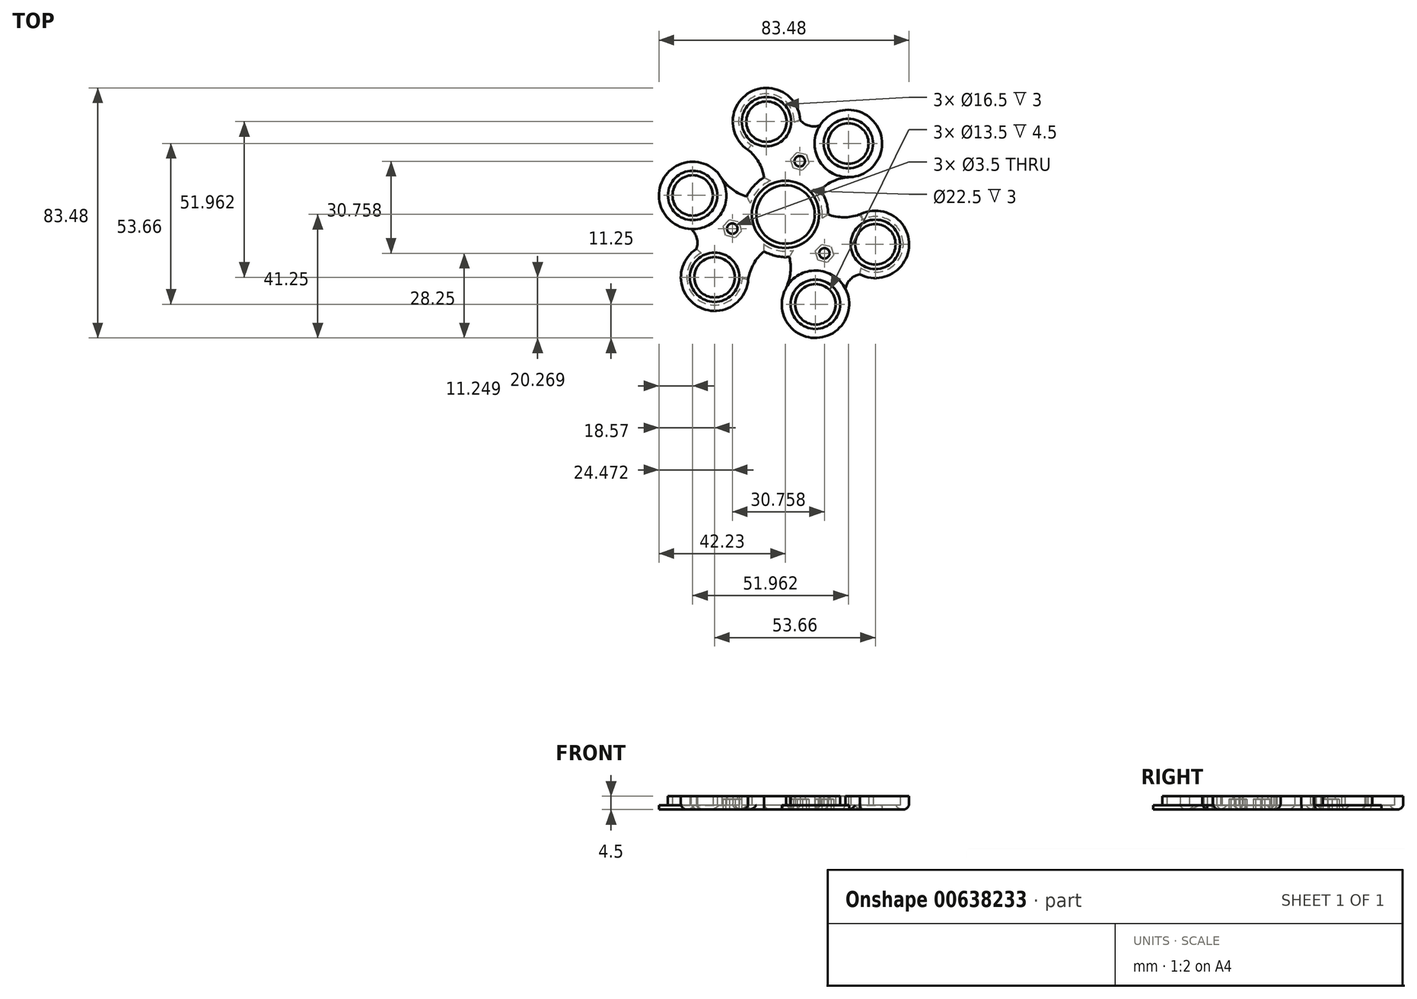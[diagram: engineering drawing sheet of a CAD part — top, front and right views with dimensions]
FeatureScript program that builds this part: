
annotation { "Feature Type Name" : "Feature", "Feature Type Description" : "" }
export const myFeature = defineFeature(function(context is Context, id is Id, definition is map)
    precondition{}
    {
        {
            assignVariable(context, id + "F0", {"name" : "OuterBearingHeight", "anyValue" : 5});
        }
        {
            assignVariable(context, id + "F1", {"name" : "CenterBearingHeight", "anyValue" : 7});
        }
        {
            var Q0;
            Q0=qCreatedBy(makeId("Top.planeOp"),FACE);
            var sketch = newSketch(context, id + "F2", { "sketchPlane" : qUnion([Q0])});
            skCircle(sketch, "E0", {"center": v(0, 0) * mm, "radius": 11.25 * mm});
            skCircle(sketch, "E1", {"center": v(0, 0) * mm, "radius": 9.75 * mm});
            skCircle(sketch, "E2", {"center": v(30, -10) * mm, "radius": 8.25 * mm});
            skCircle(sketch, "E3", {"center": v(30, -10) * mm, "radius": 6.75 * mm});
            skCircle(sketch, "E4", {"center": v(0, 0) * mm, "radius": 14.25 * mm});
            skCircle(sketch, "E5", {"center": v(30, -10) * mm, "radius": 11.25 * mm});
            skArc(sketch, "E6", {"start": v(14.25, 0) * mm, "mid": v(19.63, -0.96) * mm, "end": v(25, 0.08) * mm});
            skCircle(sketch, "E7.MirrorC", {"center": v(10, -30) * mm, "radius": 11.25 * mm});
            skCircle(sketch, "E8.MirrorC", {"center": v(10, -30) * mm, "radius": 8.25 * mm});
            skCircle(sketch, "E9.MirrorC", {"center": v(10, -30) * mm, "radius": 6.75 * mm});
            skArc(sketch, "E10.MirrorCS", {"start": v(1.27, -14.2) * mm, "mid": v(1.6, -19.87) * mm, "end": v(-0.2, -25.25) * mm});
            skArc(sketch, "E11", {"start": v(24.85, -20) * mm, "mid": v(21.66, -21.66) * mm, "end": v(20, -24.85) * mm});
            skCircle(sketch, "E12", {"center": v(13, -13) * mm, "radius": 1.75 * mm});
            skCircle(sketch, "E13.cCircle", {"center": v(13, -13) * mm, "radius": 2.75 * mm, "construction": true});
            skLineSegment(sketch, "E13.0", {"start": v(13.92, -16.04) * mm, "end": v(10.83, -15.31) * mm});
            skLineSegment(sketch, "E13.1", {"start": v(10.83, -15.31) * mm, "end": v(9.9, -12.27) * mm});
            skLineSegment(sketch, "E13.2", {"start": v(9.9, -12.27) * mm, "end": v(12.08, -9.96) * mm});
            skLineSegment(sketch, "E13.3", {"start": v(12.08, -9.96) * mm, "end": v(15.17, -10.69) * mm});
            skLineSegment(sketch, "E13.4", {"start": v(15.17, -10.69) * mm, "end": v(16.1, -13.73) * mm});
            skLineSegment(sketch, "E13.5", {"start": v(16.1, -13.73) * mm, "end": v(13.92, -16.04) * mm});
            skLineSegment(sketch, "E14.1.0", {"start": v(6.93, 20.07) * mm, "end": v(7.85, 17.03) * mm});
            skCircle(sketch, "E14.1.1", {"center": v(4.76, 17.76) * mm, "radius": 2.75 * mm, "construction": true});
            skLineSegment(sketch, "E14.1.2", {"start": v(7.85, 17.03) * mm, "end": v(5.67, 14.72) * mm});
            skLineSegment(sketch, "E14.1.3", {"start": v(5.67, 14.72) * mm, "end": v(2.58, 15.44) * mm});
            skLineSegment(sketch, "E14.1.4", {"start": v(2.58, 15.44) * mm, "end": v(1.67, 18.48) * mm});
            skLineSegment(sketch, "E14.1.5", {"start": v(1.67, 18.48) * mm, "end": v(3.84, 20.8) * mm});
            skLineSegment(sketch, "E14.1.6", {"start": v(3.84, 20.8) * mm, "end": v(6.93, 20.07) * mm});
            skCircle(sketch, "E14.1.7", {"center": v(-6.34, 30.98) * mm, "radius": 6.75 * mm});
            skCircle(sketch, "E14.1.8", {"center": v(-6.34, 30.98) * mm, "radius": 8.25 * mm});
            skCircle(sketch, "E14.1.9", {"center": v(-6.34, 30.98) * mm, "radius": 11.25 * mm});
            skArc(sketch, "E14.1.10", {"start": v(4.9, 31.52) * mm, "mid": v(7.93, 29.6) * mm, "end": v(11.52, 29.74) * mm});
            skArc(sketch, "E14.1.11", {"start": v(-7.12, 12.34) * mm, "mid": v(-8.99, 17.48) * mm, "end": v(-12.57, 21.61) * mm});
            skArc(sketch, "E14.1.12", {"start": v(11.66, 8.2) * mm, "mid": v(16.4, 11.32) * mm, "end": v(21.97, 12.45) * mm});
            skCircle(sketch, "E14.1.13", {"center": v(20.98, 23.66) * mm, "radius": 11.25 * mm});
            skCircle(sketch, "E14.1.14", {"center": v(20.98, 23.66) * mm, "radius": 8.25 * mm});
            skCircle(sketch, "E14.1.15", {"center": v(20.98, 23.66) * mm, "radius": 6.75 * mm});
            skLineSegment(sketch, "E14.2.0", {"start": v(-20.85, -4.03) * mm, "end": v(-18.67, -1.72) * mm});
            skCircle(sketch, "E14.2.1", {"center": v(-17.76, -4.76) * mm, "radius": 2.75 * mm, "construction": true});
            skLineSegment(sketch, "E14.2.2", {"start": v(-18.67, -1.72) * mm, "end": v(-15.58, -2.44) * mm});
            skLineSegment(sketch, "E14.2.3", {"start": v(-15.58, -2.44) * mm, "end": v(-14.67, -5.48) * mm});
            skLineSegment(sketch, "E14.2.4", {"start": v(-14.67, -5.48) * mm, "end": v(-16.84, -7.8) * mm});
            skLineSegment(sketch, "E14.2.5", {"start": v(-16.84, -7.8) * mm, "end": v(-19.93, -7.07) * mm});
            skLineSegment(sketch, "E14.2.6", {"start": v(-19.93, -7.07) * mm, "end": v(-20.85, -4.03) * mm});
            skCircle(sketch, "E14.2.7", {"center": v(-23.66, -20.98) * mm, "radius": 6.75 * mm});
            skCircle(sketch, "E14.2.8", {"center": v(-23.66, -20.98) * mm, "radius": 8.25 * mm});
            skCircle(sketch, "E14.2.9", {"center": v(-23.66, -20.98) * mm, "radius": 11.25 * mm});
            skArc(sketch, "E14.2.10", {"start": v(-29.74, -11.52) * mm, "mid": v(-29.6, -7.93) * mm, "end": v(-31.52, -4.9) * mm});
            skArc(sketch, "E14.2.11", {"start": v(-7.13, -12.34) * mm, "mid": v(-10.65, -16.52) * mm, "end": v(-12.43, -21.69) * mm});
            skArc(sketch, "E14.2.12", {"start": v(-12.93, 6) * mm, "mid": v(-18, 8.55) * mm, "end": v(-21.77, 12.8) * mm});
            skCircle(sketch, "E14.2.13", {"center": v(-30.98, 6.34) * mm, "radius": 11.25 * mm});
            skCircle(sketch, "E14.2.14", {"center": v(-30.98, 6.34) * mm, "radius": 8.25 * mm});
            skCircle(sketch, "E14.2.15", {"center": v(-30.98, 6.34) * mm, "radius": 6.75 * mm});
            skCircle(sketch, "E15", {"center": v(-17.76, -4.76) * mm, "radius": 1.75 * mm});
            skCircle(sketch, "E16", {"center": v(4.76, 17.76) * mm, "radius": 1.75 * mm});
            skSolve(sketch);
        }
        {
            var Q0;
            Q0=makeQuery(id+"F2.imprint","IMPRINT",FACE,{"disambiguationData":[TD([[makeQuery(id+"F2.imprint","IMPRINT",EDGE,{"derivedFrom":sQuery(id+"F2.wireOp",EDGE,"E0")}),-1.0]])]});
            var Q1;
            Q1=makeQuery(id+"F2.imprint","IMPRINT",FACE,{"disambiguationData":[TD([[makeQuery(id+"F2.imprint","IMPRINT",EDGE,{"derivedFrom":sQuery(id+"F2.wireOp",EDGE,"8bcb8120-0ba0-4aea-ab6e-afe790873060.2.4")}),1.0]])]});
            var Q2;
            Q2=makeQuery(id+"F2.imprint","IMPRINT",FACE,{"disambiguationData":[TD([[makeQuery(id+"F2.imprint","IMPRINT",EDGE,{"derivedFrom":sQuery(id+"F2.wireOp",EDGE,"77096406-894a-42e3-b711-8bd3589b9249.0")}),1.0]])]});
            var Q3;
            Q3=makeQuery(id+"F2.imprint","IMPRINT",FACE,{"disambiguationData":[TD([[makeQuery(id+"F2.imprint","IMPRINT",EDGE,{"derivedFrom":sQuery(id+"F2.wireOp",EDGE,"8bcb8120-0ba0-4aea-ab6e-afe790873060.2.11")}),-1.0]])]});
            var Q4;
            Q4=makeQuery(id+"F2.imprint","IMPRINT",FACE,{"disambiguationData":[TD([[makeQuery(id+"F2.imprint","IMPRINT",EDGE,{"derivedFrom":sQuery(id+"F2.wireOp",EDGE,"8bcb8120-0ba0-4aea-ab6e-afe790873060.1.4")}),1.0]])]});
            var Q5;
            Q5=makeQuery(id+"F2.imprint","IMPRINT",FACE,{"disambiguationData":[TD([[makeQuery(id+"F2.imprint","IMPRINT",EDGE,{"derivedFrom":sQuery(id+"F2.wireOp",EDGE,"8bcb8120-0ba0-4aea-ab6e-afe790873060.1.11")}),-1.0]])]});
            var Q6;
            Q6=makeQuery(id+"F2.imprint","IMPRINT",FACE,{"disambiguationData":[TD([[makeQuery(id+"F2.imprint","IMPRINT",EDGE,{"derivedFrom":sQuery(id+"F2.wireOp",EDGE,"E2")}),-1.0]])]});
            var Q7;
            {var subQ0=sQuery(id+"F2.wireOp",EDGE,"aIkXae3d-mRoF-3wDr-qNRh-ahO2MIR5sPZY");var subQ1=sQuery(id+"F2.wireOp",EDGE,"E5");var subQ2=makeQuery(id+"F2.imprint","INTERSECT",VERTEX,{"disambiguationData":[OD(0.0)],"derivedFrom":[subQ1,subQ0]});Q7=makeQuery(id+"F2.imprint","IMPRINT",FACE,{"disambiguationData":[TD([[makeQuery(id+"F2.imprint","IMPRINT",EDGE,{"disambiguationData":[TD([[subQ2,1.0]])],"derivedFrom":subQ1}),1.0]])]});}
            var Q8;
            {var subQ0=sQuery(id+"F2.wireOp",EDGE,"8bcb8120-0ba0-4aea-ab6e-afe790873060.2.2");var subQ1=sQuery(id+"F2.wireOp",EDGE,"8bcb8120-0ba0-4aea-ab6e-afe790873060.2.1");var subQ2=makeQuery(id+"F2.imprint","INTERSECT",VERTEX,{"disambiguationData":[OD(0.0)],"derivedFrom":[subQ1,subQ0]});Q8=makeQuery(id+"F2.imprint","IMPRINT",FACE,{"disambiguationData":[TD([[makeQuery(id+"F2.imprint","IMPRINT",EDGE,{"disambiguationData":[TD([[subQ2,1.0]])],"derivedFrom":subQ1}),-1.0]])]});}
            var Q9;
            {var subQ0=sQuery(id+"F2.wireOp",EDGE,"8bcb8120-0ba0-4aea-ab6e-afe790873060.1.2");var subQ1=sQuery(id+"F2.wireOp",EDGE,"8bcb8120-0ba0-4aea-ab6e-afe790873060.1.1");var subQ2=makeQuery(id+"F2.imprint","INTERSECT",VERTEX,{"disambiguationData":[OD(0.0)],"derivedFrom":[subQ1,subQ0]});Q9=makeQuery(id+"F2.imprint","IMPRINT",FACE,{"disambiguationData":[TD([[makeQuery(id+"F2.imprint","IMPRINT",EDGE,{"disambiguationData":[TD([[subQ2,1.0]])],"derivedFrom":subQ1}),-1.0]])]});}
            var Q10;
            Q10=makeQuery(id+"F2.imprint","IMPRINT",FACE,{"disambiguationData":[TD([[makeQuery(id+"F2.imprint","IMPRINT",EDGE,{"derivedFrom":sQuery(id+"F2.wireOp",EDGE,"E8.MirrorC")}),1.0]])]});
            var Q11;
            {var subQ5=sQuery(id+"F2.wireOp",EDGE,"E11");Q11=makeQuery(id+"F2.imprint","IMPRINT",FACE,{"disambiguationData":[TD([[makeQuery(id+"F2.imprint","IMPRINT",EDGE,{"derivedFrom":subQ5}),-1.0]])]});}
            var Q12;
            Q12=makeQuery(id+"F2.imprint","IMPRINT",FACE,{"disambiguationData":[TD([[makeQuery(id+"F2.imprint","IMPRINT",EDGE,{"derivedFrom":sQuery(id+"F2.wireOp",EDGE,"E14.2.0")}),1.0]])]});
            var Q13;
            Q13=makeQuery(id+"F2.imprint","IMPRINT",FACE,{"disambiguationData":[TD([[makeQuery(id+"F2.imprint","IMPRINT",EDGE,{"derivedFrom":sQuery(id+"F2.wireOp",EDGE,"E14.1.0")}),1.0]])]});
            var Q14;
            Q14=makeQuery(id+"F2.imprint","IMPRINT",FACE,{"disambiguationData":[TD([[makeQuery(id+"F2.imprint","IMPRINT",EDGE,{"derivedFrom":sQuery(id+"F2.wireOp",EDGE,"E14.1.8")}),-1.0]])]});
            var Q15;
            Q15=makeQuery(id+"F2.imprint","IMPRINT",FACE,{"disambiguationData":[TD([[makeQuery(id+"F2.imprint","IMPRINT",EDGE,{"derivedFrom":sQuery(id+"F2.wireOp",EDGE,"E14.2.14")}),1.0]])]});
            var Q16;
            Q16=makeQuery(id+"F2.imprint","IMPRINT",FACE,{"disambiguationData":[TD([[makeQuery(id+"F2.imprint","IMPRINT",EDGE,{"derivedFrom":sQuery(id+"F2.wireOp",EDGE,"E14.2.8")}),-1.0]])]});
            var Q17;
            Q17=makeQuery(id+"F2.imprint","IMPRINT",FACE,{"disambiguationData":[TD([[makeQuery(id+"F2.imprint","IMPRINT",EDGE,{"derivedFrom":sQuery(id+"F2.wireOp",EDGE,"E14.1.14")}),1.0]])]});
            var Q18;
            {var subQ0=sQuery(id+"F2.wireOp",EDGE,"E10.MirrorCS");var subQ1=sQuery(id+"F2.wireOp",EDGE,"E7.MirrorC");var subQ2=makeQuery(id+"F2.imprint","INTERSECT",VERTEX,{"disambiguationData":[OD(0.0)],"derivedFrom":[subQ1,subQ0]});Q18=makeQuery(id+"F2.imprint","IMPRINT",FACE,{"disambiguationData":[TD([[makeQuery(id+"F2.imprint","IMPRINT",EDGE,{"disambiguationData":[TD([[subQ2,-1.0]])],"derivedFrom":subQ1}),-1.0]])]});}
            var Q19;
            {var subQ0=sQuery(id+"F2.wireOp",EDGE,"E14.2.13");var subQ1=sQuery(id+"F2.wireOp",EDGE,"E14.2.12");var subQ2=makeQuery(id+"F2.imprint","INTERSECT",VERTEX,{"disambiguationData":[OD(0.0)],"derivedFrom":[subQ1,subQ0]});Q19=makeQuery(id+"F2.imprint","IMPRINT",FACE,{"disambiguationData":[TD([[makeQuery(id+"F2.imprint","IMPRINT",EDGE,{"disambiguationData":[TD([[subQ2,1.0]])],"derivedFrom":subQ1}),-1.0]])]});}
            var Q20;
            {var subQ0=sQuery(id+"F2.wireOp",EDGE,"E14.1.13");var subQ1=sQuery(id+"F2.wireOp",EDGE,"E14.1.12");var subQ2=makeQuery(id+"F2.imprint","INTERSECT",VERTEX,{"disambiguationData":[OD(0.0)],"derivedFrom":[subQ1,subQ0]});Q20=makeQuery(id+"F2.imprint","IMPRINT",FACE,{"disambiguationData":[TD([[makeQuery(id+"F2.imprint","IMPRINT",EDGE,{"disambiguationData":[TD([[subQ2,1.0]])],"derivedFrom":subQ1}),-1.0]])]});}
            var Q21;
            {var subQ3=sQuery(id+"F2.wireOp",EDGE,"E4");var subQ5=sQuery(id+"F2.wireOp",EDGE,"E10.MirrorCS");var subQ9=makeQuery(id+"F2.imprint","INTERSECT",VERTEX,{"derivedFrom":[subQ3,subQ5]});Q21=makeQuery(id+"F2.imprint","IMPRINT",FACE,{"disambiguationData":[TD([[makeQuery(id+"F2.imprint","IMPRINT",EDGE,{"disambiguationData":[TD([[subQ9,-1.0]])],"derivedFrom":subQ3}),-1.0]])]});}
            var Q22;
            {var subQ6=sQuery(id+"F2.wireOp",EDGE,"E14.2.3");Q22=makeQuery(id+"F2.imprint","IMPRINT",FACE,{"disambiguationData":[TD([[makeQuery(id+"F2.imprint","IMPRINT",EDGE,{"derivedFrom":subQ6}),1.0]])]});}
            var Q23;
            {var subQ0=sQuery(id+"F2.wireOp",EDGE,"E14.1.3");Q23=makeQuery(id+"F2.imprint","IMPRINT",FACE,{"disambiguationData":[TD([[makeQuery(id+"F2.imprint","IMPRINT",EDGE,{"derivedFrom":subQ0}),1.0]])]});}
            extrude(context, id + "F3", {"entities" : qUnion([Q0, Q1, Q2, Q3, Q4, Q5, Q6, Q7, Q8, Q9, Q10, Q11, Q12, Q13, Q14, Q15, Q16, Q17, Q18, Q19, Q20, Q21, Q22, Q23]), "depth" : ((getVariable(context, 'CenterBearingHeight') / 2) + 1) * mm, "offsetDistance" : 25 * mm});
        }
        {
            var Q0;
            Q0=makeQuery(id+"F2.imprint","IMPRINT",FACE,{"disambiguationData":[TD([[makeQuery(id+"F2.imprint","IMPRINT",EDGE,{"derivedFrom":sQuery(id+"F2.wireOp",EDGE,"E2")}),1.0]])]});
            var Q1;
            Q1=makeQuery(id+"F2.imprint","IMPRINT",FACE,{"disambiguationData":[TD([[makeQuery(id+"F2.imprint","IMPRINT",EDGE,{"derivedFrom":sQuery(id+"F2.wireOp",EDGE,"8bcb8120-0ba0-4aea-ab6e-afe790873060.2.11")}),1.0]])]});
            var Q2;
            Q2=makeQuery(id+"F2.imprint","IMPRINT",FACE,{"disambiguationData":[TD([[makeQuery(id+"F2.imprint","IMPRINT",EDGE,{"derivedFrom":sQuery(id+"F2.wireOp",EDGE,"8bcb8120-0ba0-4aea-ab6e-afe790873060.1.11")}),1.0]])]});
            var Q3;
            Q3=makeQuery(id+"F2.imprint","IMPRINT",FACE,{"disambiguationData":[TD([[makeQuery(id+"F2.imprint","IMPRINT",EDGE,{"derivedFrom":sQuery(id+"F2.wireOp",EDGE,"E14.1.7")}),-1.0]])]});
            var Q4;
            Q4=makeQuery(id+"F2.imprint","IMPRINT",FACE,{"disambiguationData":[TD([[makeQuery(id+"F2.imprint","IMPRINT",EDGE,{"derivedFrom":sQuery(id+"F2.wireOp",EDGE,"E14.1.14")}),-1.0]])]});
            var Q5;
            Q5=makeQuery(id+"F2.imprint","IMPRINT",FACE,{"disambiguationData":[TD([[makeQuery(id+"F2.imprint","IMPRINT",EDGE,{"derivedFrom":sQuery(id+"F2.wireOp",EDGE,"E8.MirrorC")}),-1.0]])]});
            var Q6;
            Q6=makeQuery(id+"F2.imprint","IMPRINT",FACE,{"disambiguationData":[TD([[makeQuery(id+"F2.imprint","IMPRINT",EDGE,{"derivedFrom":sQuery(id+"F2.wireOp",EDGE,"E14.2.7")}),-1.0]])]});
            var Q7;
            Q7=makeQuery(id+"F2.imprint","IMPRINT",FACE,{"disambiguationData":[TD([[makeQuery(id+"F2.imprint","IMPRINT",EDGE,{"derivedFrom":sQuery(id+"F2.wireOp",EDGE,"E0")}),1.0]])]});
            var Q8;
            Q8=makeQuery(id+"F2.imprint","IMPRINT",FACE,{"disambiguationData":[TD([[makeQuery(id+"F2.imprint","IMPRINT",EDGE,{"derivedFrom":sQuery(id+"F2.wireOp",EDGE,"E14.2.14")}),-1.0]])]});
            extrude(context, id + "F4", {"entities" : qUnion([Q0, Q1, Q2, Q3, Q4, Q5, Q6, Q7, Q8]), "operationType" : NewBodyOperationType.ADD, "depth" : (((getVariable(context, 'CenterBearingHeight') / 2) + .5) - getVariable(context, 'OuterBearingHeight') / 2) * mm, "offsetDistance" : 25 * mm});
        }
        {
            var Q0;
            Q0=makeQuery(id+"F2.imprint","IMPRINT",FACE,{"disambiguationData":[TD([[makeQuery(id+"F2.imprint","IMPRINT",EDGE,{"derivedFrom":sQuery(id+"F2.wireOp",EDGE,"8bcb8120-0ba0-4aea-ab6e-afe790873060.2.4")}),-1.0]])]});
            var Q1;
            Q1=makeQuery(id+"F2.imprint","IMPRINT",FACE,{"disambiguationData":[TD([[makeQuery(id+"F2.imprint","IMPRINT",EDGE,{"derivedFrom":sQuery(id+"F2.wireOp",EDGE,"mnrSd04r-Lz4n-X5wf-1ZHD-ls6KPZvvDbA1")}),-1.0]])]});
            var Q2;
            Q2=makeQuery(id+"F2.imprint","IMPRINT",FACE,{"disambiguationData":[TD([[makeQuery(id+"F2.imprint","IMPRINT",EDGE,{"derivedFrom":sQuery(id+"F2.wireOp",EDGE,"8bcb8120-0ba0-4aea-ab6e-afe790873060.1.4")}),-1.0]])]});
            var Q3;
            {var subQ0=sQuery(id+"F2.wireOp",EDGE,"E14.2.6");var subQ1=sQuery(id+"F2.wireOp",EDGE,"E14.2.5");var subQ2=makeQuery(id+"F2.imprint","INTERSECT",VERTEX,{"derivedFrom":[subQ1,subQ0]});Q3=makeQuery(id+"F2.imprint","IMPRINT",FACE,{"disambiguationData":[TD([[makeQuery(id+"F2.imprint","IMPRINT",EDGE,{"disambiguationData":[TD([[subQ2,1.0]])],"derivedFrom":subQ1}),-1.0]])]});}
            var Q4;
            {var subQ0=sQuery(id+"F2.wireOp",EDGE,"E14.2.3");Q4=makeQuery(id+"F2.imprint","IMPRINT",FACE,{"disambiguationData":[TD([[makeQuery(id+"F2.imprint","IMPRINT",EDGE,{"derivedFrom":subQ0}),-1.0]])]});}
            var Q5;
            {var subQ0=sQuery(id+"F2.wireOp",EDGE,"E14.2.0");var subQ1=sQuery(id+"F2.wireOp",EDGE,"E4");var subQ2=makeQuery(id+"F2.imprint","INTERSECT",VERTEX,{"derivedFrom":[subQ1,subQ0]});Q5=makeQuery(id+"F2.imprint","IMPRINT",FACE,{"disambiguationData":[TD([[makeQuery(id+"F2.imprint","IMPRINT",EDGE,{"disambiguationData":[TD([[subQ2,-1.0]])],"derivedFrom":subQ1}),1.0]])]});}
            var Q6;
            Q6=makeQuery(id+"F2.imprint","IMPRINT",FACE,{"disambiguationData":[TD([[makeQuery(id+"F2.imprint","IMPRINT",EDGE,{"derivedFrom":sQuery(id+"F2.wireOp",EDGE,"E12")}),-1.0]])]});
            var Q7;
            {var subQ0=sQuery(id+"F2.wireOp",EDGE,"E13.5");var subQ1=sQuery(id+"F2.wireOp",EDGE,"E7.MirrorC");var subQ2=makeQuery(id+"F2.imprint","INTERSECT",VERTEX,{"derivedFrom":[subQ1,subQ0]});Q7=makeQuery(id+"F2.imprint","IMPRINT",FACE,{"disambiguationData":[TD([[makeQuery(id+"F2.imprint","IMPRINT",EDGE,{"disambiguationData":[TD([[subQ2,-1.0]])],"derivedFrom":subQ1}),-1.0]])]});}
            var Q8;
            {var subQ0=sQuery(id+"F2.wireOp",EDGE,"E13.0");var subQ1=sQuery(id+"F2.wireOp",EDGE,"E4");var subQ2=makeQuery(id+"F2.imprint","INTERSECT",VERTEX,{"derivedFrom":[subQ1,subQ0]});Q8=makeQuery(id+"F2.imprint","IMPRINT",FACE,{"disambiguationData":[TD([[makeQuery(id+"F2.imprint","IMPRINT",EDGE,{"disambiguationData":[TD([[subQ2,-1.0]])],"derivedFrom":subQ1}),1.0]])]});}
            var Q9;
            {var subQ0=sQuery(id+"F2.wireOp",EDGE,"E14.1.6");var subQ1=sQuery(id+"F2.wireOp",EDGE,"E14.1.5");var subQ2=makeQuery(id+"F2.imprint","INTERSECT",VERTEX,{"derivedFrom":[subQ1,subQ0]});Q9=makeQuery(id+"F2.imprint","IMPRINT",FACE,{"disambiguationData":[TD([[makeQuery(id+"F2.imprint","IMPRINT",EDGE,{"disambiguationData":[TD([[subQ2,1.0]])],"derivedFrom":subQ1}),-1.0]])]});}
            var Q10;
            {var subQ0=sQuery(id+"F2.wireOp",EDGE,"E14.1.3");Q10=makeQuery(id+"F2.imprint","IMPRINT",FACE,{"disambiguationData":[TD([[makeQuery(id+"F2.imprint","IMPRINT",EDGE,{"derivedFrom":subQ0}),-1.0]])]});}
            var Q11;
            {var subQ0=sQuery(id+"F2.wireOp",EDGE,"E14.1.0");var subQ1=sQuery(id+"F2.wireOp",EDGE,"E4");var subQ2=makeQuery(id+"F2.imprint","INTERSECT",VERTEX,{"derivedFrom":[subQ1,subQ0]});Q11=makeQuery(id+"F2.imprint","IMPRINT",FACE,{"disambiguationData":[TD([[makeQuery(id+"F2.imprint","IMPRINT",EDGE,{"disambiguationData":[TD([[subQ2,-1.0]])],"derivedFrom":subQ1}),1.0]])]});}
            extrude(context, id + "F5", {"entities" : qUnion([Q0, Q1, Q2, Q3, Q4, Q5, Q6, Q7, Q8, Q9, Q10, Q11]), "operationType" : NewBodyOperationType.ADD, "depth" : ((getVariable(context, 'CenterBearingHeight') / 2) + 1) * mm, "offsetDistance" : 25 * mm, "hasSecondDirection" : true, "secondDirectionOppositeDirection" : false, "secondDirectionDepth" : 3.5 * mm});
        }
        {
            var Q0;
            Q0=makeQuery(id+"F2.imprint","IMPRINT",FACE,{"disambiguationData":[TD([[makeQuery(id+"F2.imprint","IMPRINT",EDGE,{"derivedFrom":sQuery(id+"F2.wireOp",EDGE,"E0")}),1.0]])]});
            extrude(context, id + "F6", {"entities" : qUnion([Q0]), "operationType" : NewBodyOperationType.ADD, "depth" : 1 * mm, "offsetDistance" : 25 * mm});
        }
        {
            var Q0;
            Q0=makeQuery(id+"F3.opExtrude","CAP_EDGE",EDGE,{"disambiguationData":[OSD([sQuery(id+"F2.wireOp",EDGE,"E14.2.13")])],"isStart":true});
            var Q1;
            Q1=makeQuery(id+"F3.opExtrude","CAP_EDGE",EDGE,{"disambiguationData":[OSD([sQuery(id+"F2.wireOp",EDGE,"E14.2.12")])],"isStart":true});
            var Q2;
            {var subQ0=sQuery(id+"F2.wireOp",EDGE,"E4");Q2=makeQuery(id+"F3.opExtrude","CAP_EDGE",EDGE,{"disambiguationData":[OSD([subQ0]),TDD([makeQuery(id+"F2.imprint","IMPRINT",EDGE,{"disambiguationData":[TD([[makeQuery(id+"F2.imprint","INTERSECT",VERTEX,{"derivedFrom":[subQ0,sQuery(id+"F2.wireOp",EDGE,"E14.1.11")]}),-1.0]])],"derivedFrom":subQ0})])],"isStart":true});}
            var Q3;
            Q3=makeQuery(id+"F3.opExtrude","CAP_EDGE",EDGE,{"disambiguationData":[OSD([sQuery(id+"F2.wireOp",EDGE,"E14.2.10")])],"isStart":true});
            var Q4;
            Q4=makeQuery(id+"F3.opExtrude","CAP_EDGE",EDGE,{"disambiguationData":[OSD([sQuery(id+"F2.wireOp",EDGE,"E14.2.9")])],"isStart":true});
            var Q5;
            {var subQ0=sQuery(id+"F2.wireOp",EDGE,"E4");Q5=makeQuery(id+"F3.opExtrude","CAP_EDGE",EDGE,{"disambiguationData":[OSD([subQ0]),TDD([makeQuery(id+"F2.imprint","IMPRINT",EDGE,{"disambiguationData":[TD([[makeQuery(id+"F2.imprint","INTERSECT",VERTEX,{"derivedFrom":[subQ0,sQuery(id+"F2.wireOp",EDGE,"E10.MirrorCS")]}),1.0]])],"derivedFrom":subQ0})])],"isStart":true});}
            var Q6;
            Q6=makeQuery(id+"F3.opExtrude","CAP_EDGE",EDGE,{"disambiguationData":[OSD([sQuery(id+"F2.wireOp",EDGE,"E10.MirrorCS")])],"isStart":true});
            var Q7;
            Q7=makeQuery(id+"F3.opExtrude","CAP_EDGE",EDGE,{"disambiguationData":[OSD([sQuery(id+"F2.wireOp",EDGE,"E7.MirrorC")])],"isStart":true});
            var Q8;
            Q8=makeQuery(id+"F3.opExtrude","CAP_EDGE",EDGE,{"disambiguationData":[OSD([sQuery(id+"F2.wireOp",EDGE,"E11")])],"isStart":true});
            var Q9;
            Q9=makeQuery(id+"F3.opExtrude","CAP_EDGE",EDGE,{"disambiguationData":[OSD([sQuery(id+"F2.wireOp",EDGE,"E5")])],"isStart":true});
            var Q10;
            Q10=makeQuery(id+"F3.opExtrude","CAP_EDGE",EDGE,{"disambiguationData":[OSD([sQuery(id+"F2.wireOp",EDGE,"E6")])],"isStart":true});
            var Q11;
            {var subQ0=sQuery(id+"F2.wireOp",EDGE,"E4");Q11=makeQuery(id+"F3.opExtrude","CAP_EDGE",EDGE,{"disambiguationData":[OSD([subQ0]),TDD([makeQuery(id+"F2.imprint","IMPRINT",EDGE,{"disambiguationData":[TD([[makeQuery(id+"F2.imprint","INTERSECT",VERTEX,{"derivedFrom":[subQ0,sQuery(id+"F2.wireOp",EDGE,"E6")]}),-1.0]])],"derivedFrom":subQ0})])],"isStart":true});}
            var Q12;
            Q12=makeQuery(id+"F3.opExtrude","CAP_EDGE",EDGE,{"disambiguationData":[OSD([sQuery(id+"F2.wireOp",EDGE,"E14.1.12")])],"isStart":true});
            var Q13;
            Q13=makeQuery(id+"F3.opExtrude","CAP_EDGE",EDGE,{"disambiguationData":[OSD([sQuery(id+"F2.wireOp",EDGE,"E14.1.11")])],"isStart":true});
            var Q14;
            Q14=makeQuery(id+"F3.opExtrude","CAP_EDGE",EDGE,{"disambiguationData":[OSD([sQuery(id+"F2.wireOp",EDGE,"E14.1.10")])],"isStart":true});
            var Q15;
            Q15=makeQuery(id+"F3.opExtrude","CAP_EDGE",EDGE,{"disambiguationData":[OSD([sQuery(id+"F2.wireOp",EDGE,"E14.1.9")])],"isStart":true});
            var Q16;
            Q16=makeQuery(id+"F3.opExtrude","CAP_EDGE",EDGE,{"disambiguationData":[OSD([sQuery(id+"F2.wireOp",EDGE,"E14.1.13")])],"isStart":true});
            fillet(context, id + "F7", {"entities" : qUnion([Q0, Q1, Q2, Q3, Q4, Q5, Q6, Q7, Q8, Q9, Q10, Q11, Q12, Q13, Q14, Q15, Q16]), "radius" : 2 * mm, "tangentPropagation" : true, "allowEdgeOverflow" : false});
        }
        {
            var Q0;
            Q0=makeQuery(id+"F6.opExtrude","CAP_EDGE",EDGE,{"disambiguationData":[OSD([sQuery(id+"F2.wireOp",EDGE,"E1")])],"isStart":true});
            var Q1;
            Q1=makeQuery(id+"F4.opExtrude","CAP_EDGE",EDGE,{"disambiguationData":[OSD([sQuery(id+"F2.wireOp",EDGE,"8bcb8120-0ba0-4aea-ab6e-afe790873060.1.12")])],"isStart":true});
            var Q2;
            Q2=makeQuery(id+"F4.opExtrude","CAP_EDGE",EDGE,{"disambiguationData":[OSD([sQuery(id+"F2.wireOp",EDGE,"E3")])],"isStart":true});
            var Q3;
            Q3=makeQuery(id+"F4.opExtrude","CAP_EDGE",EDGE,{"disambiguationData":[OSD([sQuery(id+"F2.wireOp",EDGE,"8bcb8120-0ba0-4aea-ab6e-afe790873060.2.12")])],"isStart":true});
            var Q4;
            Q4=makeQuery(id+"F4.opExtrude","CAP_EDGE",EDGE,{"disambiguationData":[OSD([sQuery(id+"F2.wireOp",EDGE,"E14.2.7")])],"isStart":true});
            var Q5;
            Q5=makeQuery(id+"F4.opExtrude","CAP_EDGE",EDGE,{"disambiguationData":[OSD([sQuery(id+"F2.wireOp",EDGE,"E14.2.15")])],"isStart":true});
            var Q6;
            Q6=makeQuery(id+"F4.opExtrude","CAP_EDGE",EDGE,{"disambiguationData":[OSD([sQuery(id+"F2.wireOp",EDGE,"E9.MirrorC")])],"isStart":true});
            var Q7;
            Q7=makeQuery(id+"F4.opExtrude","CAP_EDGE",EDGE,{"disambiguationData":[OSD([sQuery(id+"F2.wireOp",EDGE,"E1")])],"isStart":true});
            var Q8;
            Q8=makeQuery(id+"F4.opExtrude","CAP_EDGE",EDGE,{"disambiguationData":[OSD([sQuery(id+"F2.wireOp",EDGE,"E14.1.15")])],"isStart":true});
            var Q9;
            Q9=makeQuery(id+"F4.opExtrude","CAP_EDGE",EDGE,{"disambiguationData":[OSD([sQuery(id+"F2.wireOp",EDGE,"E14.1.7")])],"isStart":true});
            fillet(context, id + "F8", {"entities" : qUnion([Q0, Q1, Q2, Q3, Q4, Q5, Q6, Q7, Q8, Q9]), "radius" : 3 * mm, "tangentPropagation" : true, "allowEdgeOverflow" : false});
        }
        {
            var Q0;
            Q0=makeQuery(id+"F3.opExtrude","SWEPT_EDGE",EDGE,{"disambiguationData":[OSD([sQuery(id+"F2.wireOp",EDGE,"8bcb8120-0ba0-4aea-ab6e-afe790873060.1.0"),sQuery(id+"F2.wireOp",EDGE,"8bcb8120-0ba0-4aea-ab6e-afe790873060.1.2")])]});
            var Q1;
            Q1=makeQuery(id+"F3.opExtrude","SWEPT_EDGE",EDGE,{"disambiguationData":[OSD([sQuery(id+"F2.wireOp",EDGE,"8bcb8120-0ba0-4aea-ab6e-afe790873060.2.0"),sQuery(id+"F2.wireOp",EDGE,"8bcb8120-0ba0-4aea-ab6e-afe790873060.2.2")])]});
            var Q2;
            Q2=makeQuery(id+"F3.opExtrude","SWEPT_EDGE",EDGE,{"disambiguationData":[OSD([sQuery(id+"F2.wireOp",EDGE,"E5"),sQuery(id+"F2.wireOp",EDGE,"E6")])]});
            fillet(context, id + "F9", {"entities" : qUnion([Q0, Q1, Q2]), "radius" : 8 * mm, "tangentPropagation" : true, "allowEdgeOverflow" : false});
        }
    });
